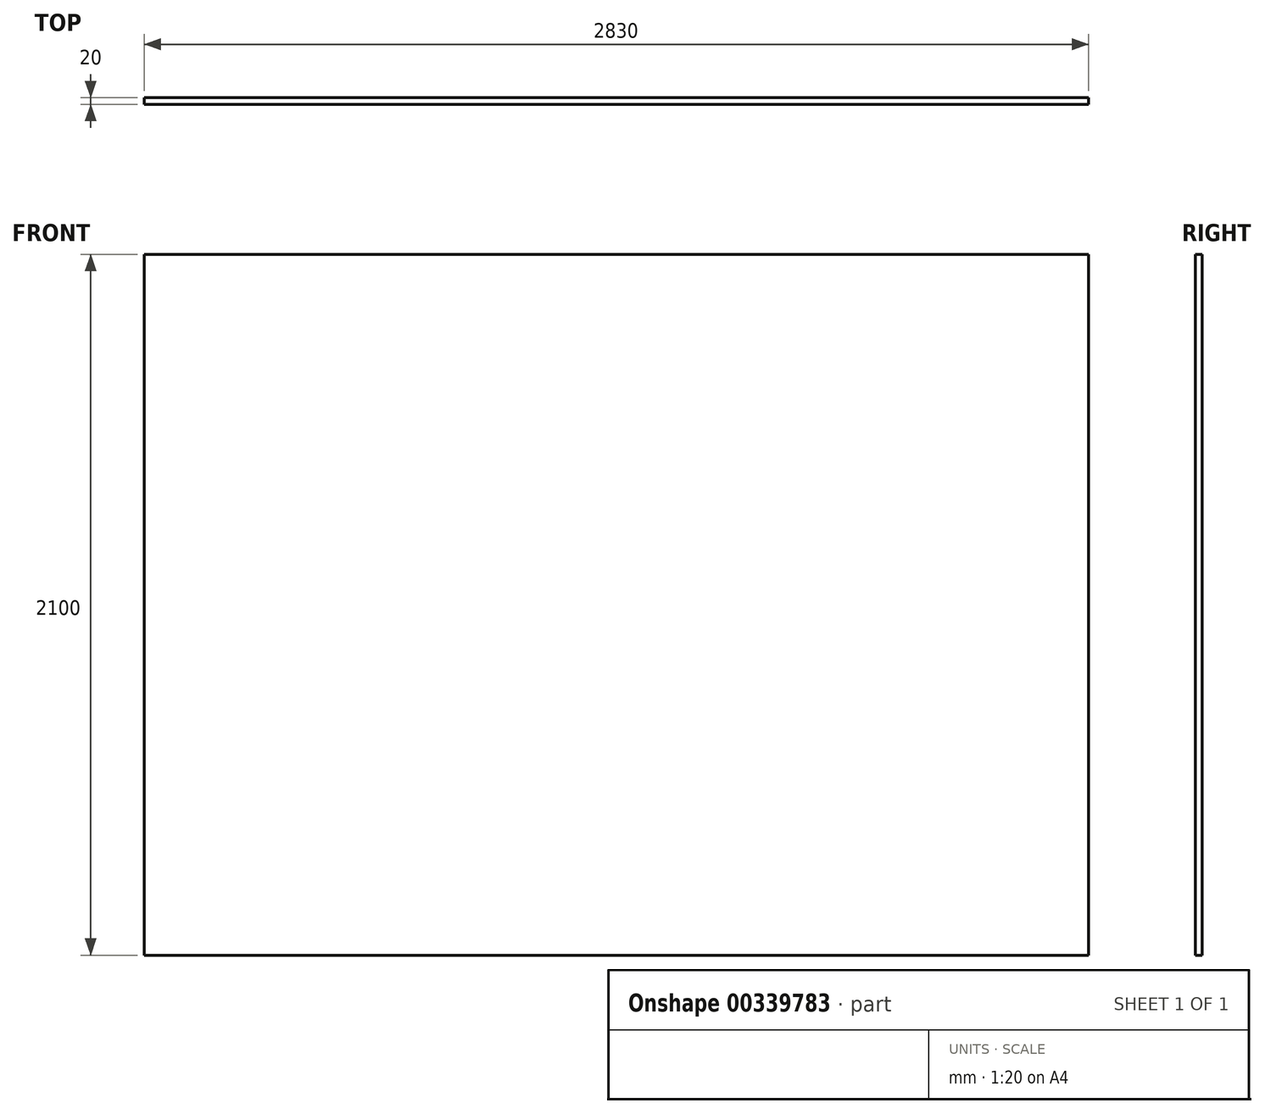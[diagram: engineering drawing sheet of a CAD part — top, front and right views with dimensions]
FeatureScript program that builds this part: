
annotation { "Feature Type Name" : "Feature", "Feature Type Description" : "" }
export const myFeature = defineFeature(function(context is Context, id is Id, definition is map)
    precondition{}
    {
        {
            var Q0;
            Q0=qCreatedBy(makeId("Front.planeOp"),FACE);
            var sketch = newSketch(context, id + "F0", { "sketchPlane" : qUnion([Q0])});
            skLineSegment(sketch, "E0.bottom", {"start": v(0, 0) * mm, "end": v(2830, 0) * mm});
            skLineSegment(sketch, "E0.top", {"start": v(0, 2100) * mm, "end": v(2830, 2100) * mm});
            skLineSegment(sketch, "E0.left", {"start": v(0, 0) * mm, "end": v(0, 2100) * mm});
            skLineSegment(sketch, "E0.right", {"start": v(2830, 0) * mm, "end": v(2830, 2100) * mm});
            skSolve(sketch);
        }
        {
            var Q0;
            Q0=makeQuery(id+"F0.imprint","IMPRINT",FACE,{"disambiguationData":[TD([[makeQuery(id+"F0.imprint","IMPRINT",EDGE,{"derivedFrom":sQuery(id+"F0.wireOp",EDGE,"E0.bottom")}),1.0]])]});
            extrude(context, id + "F1", {"entities" : qUnion([Q0]), "depth" : 20 * mm});
        }
    });
